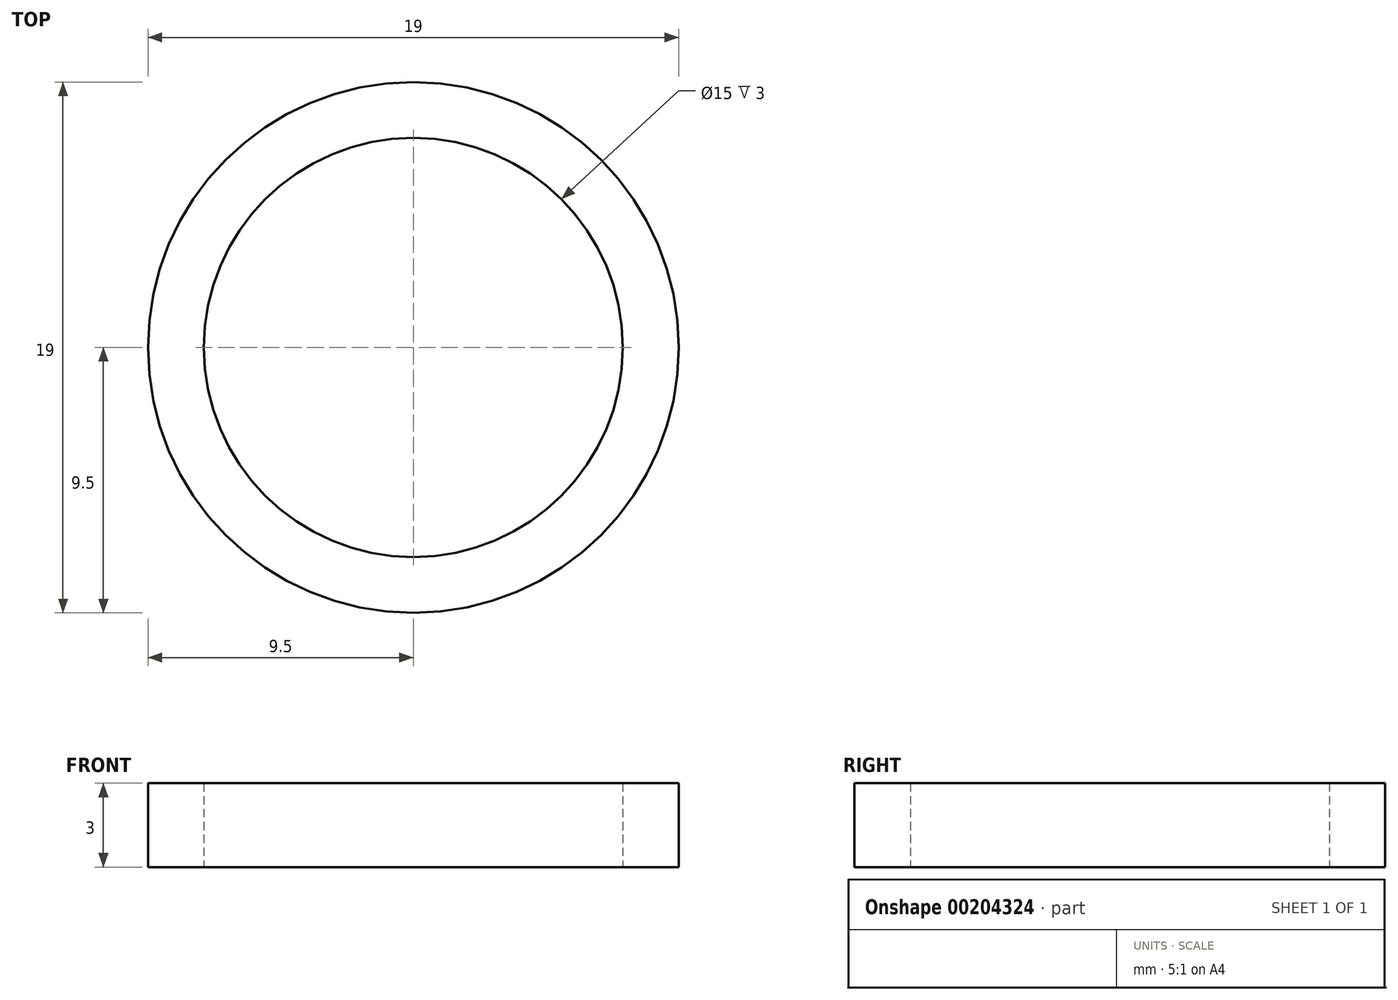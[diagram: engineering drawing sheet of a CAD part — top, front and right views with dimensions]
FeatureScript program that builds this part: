
annotation { "Feature Type Name" : "Feature", "Feature Type Description" : "" }
export const myFeature = defineFeature(function(context is Context, id is Id, definition is map)
    precondition{}
    {
        {
            var Q0;
            Q0=qCreatedBy(makeId("Top.planeOp"),FACE);
            var sketch = newSketch(context, id + "F0", { "sketchPlane" : qUnion([Q0])});
            skCircle(sketch, "E0", {"center": v(0, 0) * mm, "radius": 7.5 * mm});
            skPoint(sketch, "E1", {"position": v(-7.5, 0) * mm});
            skPoint(sketch, "E2", {"position": v(7.5, 0) * mm});
            skCircle(sketch, "E3.0", {"center": v(0, 0) * mm, "radius": 9.5 * mm});
            skSolve(sketch);
        }
        {
            var Q0;
            Q0=makeQuery(id+"F0.imprint","IMPRINT",FACE,{"disambiguationData":[TD([[makeQuery(id+"F0.imprint","IMPRINT",EDGE,{"derivedFrom":sQuery(id+"F0.wireOp",EDGE,"E0")}),-1.0]])]});
            extrude(context, id + "F1", {"entities" : qUnion([Q0]), "depth" : 3 * mm});
        }
    });
